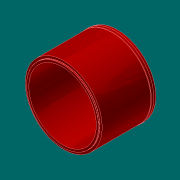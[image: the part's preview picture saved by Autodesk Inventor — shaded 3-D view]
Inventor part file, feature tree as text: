
AUTODESK INVENTOR PART (.ipt)
format: ipt  version: 2017.3 (Build 213257000, 257)  size: 146,944 bytes
history: native  units: in
note: dims shown in document units (in); Inventor stores cm internally (conversion verified against a paired STEP export)
features: extrude x4, sketch x4, chamfer x2, fillet x1
ambient origin geometry x8: Origin, YZ Plane, XZ Plane, XY Plane, X Axis, Y Axis, Z Axis, Center Point
bodies: Solid1 (feature_tree)
feature tree (11):
  extrude  "Extrusion1"  Depth=32.5in
  extrude  "Extrusion2"  Depth=22.7165in
  extrude  "Extrusion3"  Depth=1.0in
  chamfer  "Chamfer1"  Distance=1.0in
  extrude  "Extrusion4"  Depth=0.0312in TaperAngle=45.0deg
  fillet  "Fillet1"  Radius=30.48in
  chamfer  "Chamfer2"  Distance=0.5in
  sketch  "Sketch1"  dims[d0=28.5in d1=32.5in]
  sketch  "Sketch2"  dims[d2=22.7165in d3=0.0in d4=32.75in]
  sketch  "Sketch3"  dims[d5=2.0in d6=0.0in d7=32.48in d8=1.0in d9=0.0in]
  sketch  "Sketch4"  dims[d10=0.125in d11=0.125in d12=45.0deg d13=30.48in d14=0.5in d15=0.0in d16=0.0312in d17=0.0312in d18=0.125in d19=45.0deg]
